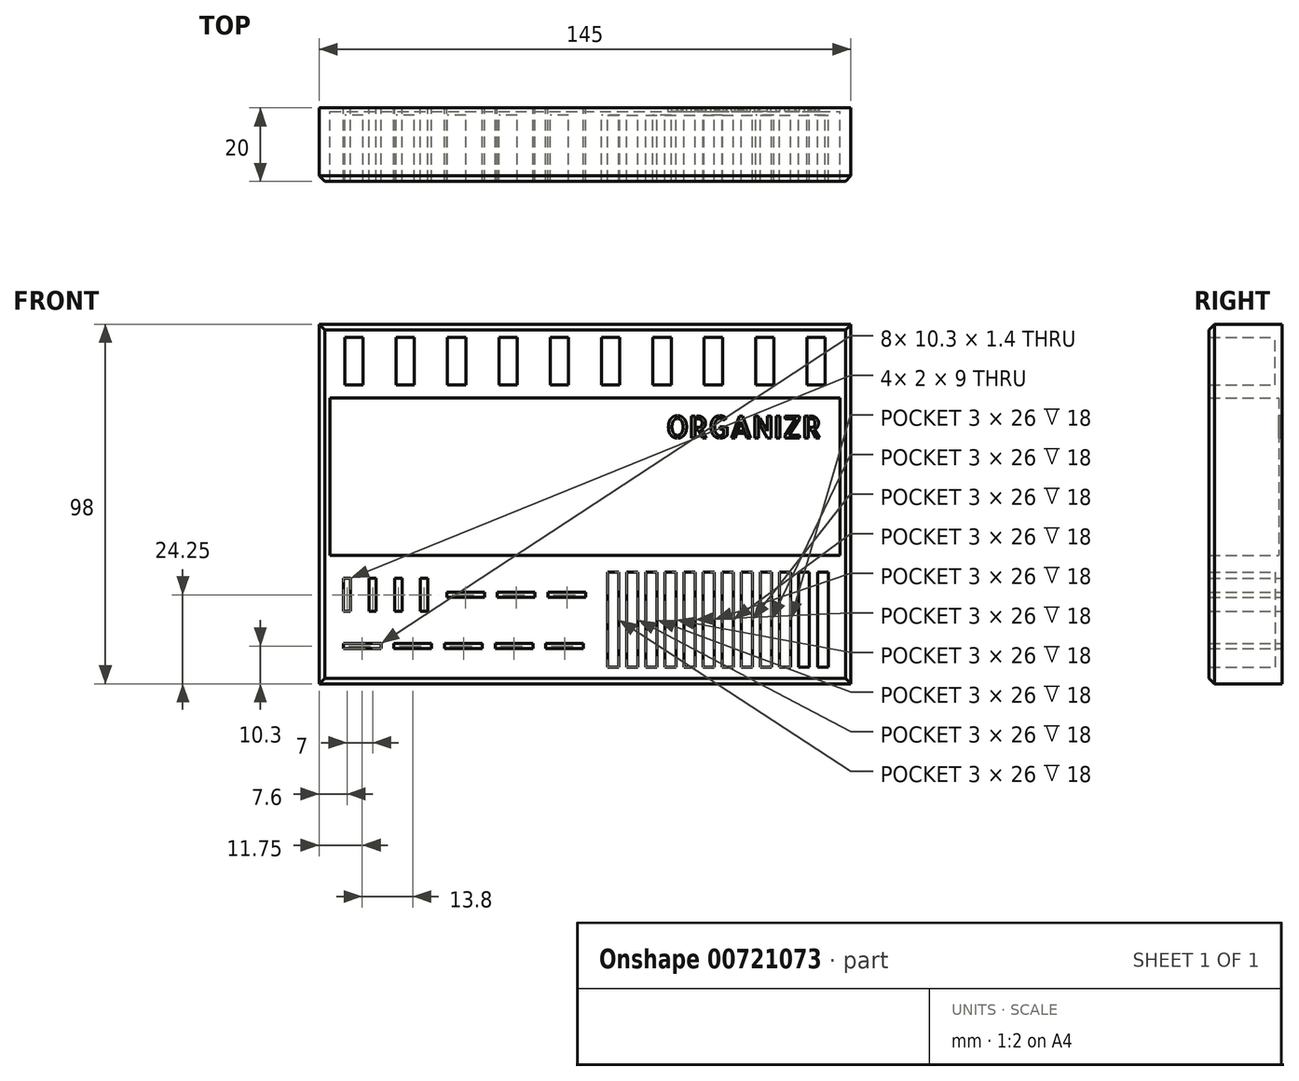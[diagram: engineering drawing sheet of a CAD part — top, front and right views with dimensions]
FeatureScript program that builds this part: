
annotation { "Feature Type Name" : "Feature", "Feature Type Description" : "" }
export const myFeature = defineFeature(function(context is Context, id is Id, definition is map)
    precondition{}
    {
        {
            var Q0;
            Q0=qCreatedBy(makeId("Front.planeOp"),FACE);
            var sketch = newSketch(context, id + "F0", { "sketchPlane" : qUnion([Q0])});
            skLineSegment(sketch, "E0.bottom", {"start": v(72.5, 49) * mm, "end": v(-72.5, 49) * mm});
            skLineSegment(sketch, "E0.top", {"start": v(72.5, -49) * mm, "end": v(-72.5, -49) * mm});
            skLineSegment(sketch, "E0.left", {"start": v(72.5, 49) * mm, "end": v(72.5, -49) * mm});
            skLineSegment(sketch, "E0.right", {"start": v(-72.5, 49) * mm, "end": v(-72.5, -49) * mm});
            skPoint(sketch, "E0.middle", {"position": v(0, 0) * mm});
            skLineSegment(sketch, "E1.bottom", {"start": v(-60.5, 32.5) * mm, "end": v(-65.5, 32.5) * mm});
            skLineSegment(sketch, "E1.top", {"start": v(-60.5, 45.5) * mm, "end": v(-65.5, 45.5) * mm});
            skLineSegment(sketch, "E1.left", {"start": v(-60.5, 32.5) * mm, "end": v(-60.5, 45.5) * mm});
            skLineSegment(sketch, "E1.right", {"start": v(-65.5, 32.5) * mm, "end": v(-65.5, 45.5) * mm});
            skPoint(sketch, "E1.middle", {"position": v(-63, 39) * mm});
            skLineSegment(sketch, "E2.bottom", {"start": v(-46.5, 32.5) * mm, "end": v(-51.5, 32.5) * mm});
            skLineSegment(sketch, "E2.top", {"start": v(-46.5, 45.5) * mm, "end": v(-51.5, 45.5) * mm});
            skLineSegment(sketch, "E2.left", {"start": v(-46.5, 32.5) * mm, "end": v(-46.5, 45.5) * mm});
            skLineSegment(sketch, "E2.right", {"start": v(-51.5, 32.5) * mm, "end": v(-51.5, 45.5) * mm});
            skLineSegment(sketch, "E3.bottom", {"start": v(-32.5, 32.5) * mm, "end": v(-37.5, 32.5) * mm});
            skLineSegment(sketch, "E3.top", {"start": v(-32.5, 45.5) * mm, "end": v(-37.5, 45.5) * mm});
            skLineSegment(sketch, "E3.left", {"start": v(-32.5, 32.5) * mm, "end": v(-32.5, 45.5) * mm});
            skLineSegment(sketch, "E3.right", {"start": v(-37.5, 32.5) * mm, "end": v(-37.5, 45.5) * mm});
            skLineSegment(sketch, "E4.bottom", {"start": v(-18.5, 32.5) * mm, "end": v(-23.5, 32.5) * mm});
            skLineSegment(sketch, "E4.top", {"start": v(-18.5, 45.5) * mm, "end": v(-23.5, 45.5) * mm});
            skLineSegment(sketch, "E4.left", {"start": v(-18.5, 32.5) * mm, "end": v(-18.5, 45.5) * mm});
            skLineSegment(sketch, "E4.right", {"start": v(-23.5, 32.5) * mm, "end": v(-23.5, 45.5) * mm});
            skLineSegment(sketch, "E5.bottom", {"start": v(-4.5, 32.5) * mm, "end": v(-9.5, 32.5) * mm});
            skLineSegment(sketch, "E5.top", {"start": v(-4.5, 45.5) * mm, "end": v(-9.5, 45.5) * mm});
            skLineSegment(sketch, "E5.left", {"start": v(-4.5, 32.5) * mm, "end": v(-4.5, 45.5) * mm});
            skLineSegment(sketch, "E5.right", {"start": v(-9.5, 32.5) * mm, "end": v(-9.5, 45.5) * mm});
            skPoint(sketch, "E5.middle", {"position": v(-7, 39) * mm});
            skLineSegment(sketch, "E6.bottom", {"start": v(9.5, 32.5) * mm, "end": v(4.5, 32.5) * mm});
            skLineSegment(sketch, "E6.top", {"start": v(9.5, 45.5) * mm, "end": v(4.5, 45.5) * mm});
            skLineSegment(sketch, "E6.left", {"start": v(9.5, 32.5) * mm, "end": v(9.5, 45.5) * mm});
            skLineSegment(sketch, "E6.right", {"start": v(4.5, 32.5) * mm, "end": v(4.5, 45.5) * mm});
            skLineSegment(sketch, "E7.bottom", {"start": v(23.5, 32.5) * mm, "end": v(18.5, 32.5) * mm});
            skLineSegment(sketch, "E7.top", {"start": v(23.5, 45.5) * mm, "end": v(18.5, 45.5) * mm});
            skLineSegment(sketch, "E7.left", {"start": v(23.5, 32.5) * mm, "end": v(23.5, 45.5) * mm});
            skLineSegment(sketch, "E7.right", {"start": v(18.5, 32.5) * mm, "end": v(18.5, 45.5) * mm});
            skLineSegment(sketch, "E8.bottom", {"start": v(37.5, 32.5) * mm, "end": v(32.5, 32.5) * mm});
            skLineSegment(sketch, "E8.top", {"start": v(37.5, 45.5) * mm, "end": v(32.5, 45.5) * mm});
            skLineSegment(sketch, "E8.left", {"start": v(37.5, 32.5) * mm, "end": v(37.5, 45.5) * mm});
            skLineSegment(sketch, "E8.right", {"start": v(32.5, 32.5) * mm, "end": v(32.5, 45.5) * mm});
            skLineSegment(sketch, "E9.bottom", {"start": v(51.5, 32.5) * mm, "end": v(46.5, 32.5) * mm});
            skLineSegment(sketch, "E9.top", {"start": v(51.5, 45.5) * mm, "end": v(46.5, 45.5) * mm});
            skLineSegment(sketch, "E9.left", {"start": v(51.5, 32.5) * mm, "end": v(51.5, 45.5) * mm});
            skLineSegment(sketch, "E9.right", {"start": v(46.5, 32.5) * mm, "end": v(46.5, 45.5) * mm});
            skLineSegment(sketch, "E10.bottom", {"start": v(65.5, 32.5) * mm, "end": v(60.5, 32.5) * mm});
            skLineSegment(sketch, "E10.top", {"start": v(65.5, 45.5) * mm, "end": v(60.5, 45.5) * mm});
            skLineSegment(sketch, "E10.left", {"start": v(65.5, 32.5) * mm, "end": v(65.5, 45.5) * mm});
            skLineSegment(sketch, "E10.right", {"start": v(60.5, 32.5) * mm, "end": v(60.5, 45.5) * mm});
            skLineSegment(sketch, "E11.bottom", {"start": v(-69.5, 29) * mm, "end": v(69.5, 29) * mm});
            skLineSegment(sketch, "E11.top", {"start": v(-69.5, -14) * mm, "end": v(69.5, -14) * mm});
            skLineSegment(sketch, "E11.left", {"start": v(-69.5, 29) * mm, "end": v(-69.5, -14) * mm});
            skLineSegment(sketch, "E11.right", {"start": v(69.5, 29) * mm, "end": v(69.5, -14) * mm});
            skLineSegment(sketch, "E12.bottom", {"start": v(63.4, -18.5) * mm, "end": v(66.4, -18.5) * mm});
            skLineSegment(sketch, "E12.top", {"start": v(63.4, -44.5) * mm, "end": v(66.4, -44.5) * mm});
            skLineSegment(sketch, "E12.left", {"start": v(63.4, -18.5) * mm, "end": v(63.4, -44.5) * mm});
            skLineSegment(sketch, "E12.right", {"start": v(66.4, -18.5) * mm, "end": v(66.4, -44.5) * mm});
            skLineSegment(sketch, "E13.bottom", {"start": v(58.2, -18.5) * mm, "end": v(61.2, -18.5) * mm});
            skLineSegment(sketch, "E13.top", {"start": v(58.2, -44.5) * mm, "end": v(61.2, -44.5) * mm});
            skLineSegment(sketch, "E13.left", {"start": v(58.2, -18.5) * mm, "end": v(58.2, -44.5) * mm});
            skLineSegment(sketch, "E13.right", {"start": v(61.2, -18.5) * mm, "end": v(61.2, -44.5) * mm});
            skLineSegment(sketch, "E14.bottom", {"start": v(53, -18.5) * mm, "end": v(56, -18.5) * mm});
            skLineSegment(sketch, "E14.top", {"start": v(53, -44.5) * mm, "end": v(56, -44.5) * mm});
            skLineSegment(sketch, "E14.left", {"start": v(53, -18.5) * mm, "end": v(53, -44.5) * mm});
            skLineSegment(sketch, "E14.right", {"start": v(56, -18.5) * mm, "end": v(56, -44.5) * mm});
            skLineSegment(sketch, "E15.bottom", {"start": v(47.8, -18.5) * mm, "end": v(50.8, -18.5) * mm});
            skLineSegment(sketch, "E15.top", {"start": v(47.8, -44.5) * mm, "end": v(50.8, -44.5) * mm});
            skLineSegment(sketch, "E15.left", {"start": v(47.8, -18.5) * mm, "end": v(47.8, -44.5) * mm});
            skLineSegment(sketch, "E15.right", {"start": v(50.8, -18.5) * mm, "end": v(50.8, -44.5) * mm});
            skLineSegment(sketch, "E16.bottom", {"start": v(42.6, -18.5) * mm, "end": v(45.6, -18.5) * mm});
            skLineSegment(sketch, "E16.top", {"start": v(42.6, -44.5) * mm, "end": v(45.6, -44.5) * mm});
            skLineSegment(sketch, "E16.left", {"start": v(42.6, -18.5) * mm, "end": v(42.6, -44.5) * mm});
            skLineSegment(sketch, "E16.right", {"start": v(45.6, -18.5) * mm, "end": v(45.6, -44.5) * mm});
            skLineSegment(sketch, "E17.bottom", {"start": v(37.4, -18.5) * mm, "end": v(40.4, -18.5) * mm});
            skLineSegment(sketch, "E17.top", {"start": v(37.4, -44.5) * mm, "end": v(40.4, -44.5) * mm});
            skLineSegment(sketch, "E17.left", {"start": v(37.4, -18.5) * mm, "end": v(37.4, -44.5) * mm});
            skLineSegment(sketch, "E17.right", {"start": v(40.4, -18.5) * mm, "end": v(40.4, -44.5) * mm});
            skLineSegment(sketch, "E18.bottom", {"start": v(32.2, -18.5) * mm, "end": v(35.2, -18.5) * mm});
            skLineSegment(sketch, "E18.top", {"start": v(32.2, -44.5) * mm, "end": v(35.2, -44.5) * mm});
            skLineSegment(sketch, "E18.left", {"start": v(32.2, -18.5) * mm, "end": v(32.2, -44.5) * mm});
            skLineSegment(sketch, "E18.right", {"start": v(35.2, -18.5) * mm, "end": v(35.2, -44.5) * mm});
            skLineSegment(sketch, "E19.bottom", {"start": v(27, -18.5) * mm, "end": v(30, -18.5) * mm});
            skLineSegment(sketch, "E19.top", {"start": v(27, -44.5) * mm, "end": v(30, -44.5) * mm});
            skLineSegment(sketch, "E19.left", {"start": v(27, -18.5) * mm, "end": v(27, -44.5) * mm});
            skLineSegment(sketch, "E19.right", {"start": v(30, -18.5) * mm, "end": v(30, -44.5) * mm});
            skLineSegment(sketch, "E20.bottom", {"start": v(21.8, -18.5) * mm, "end": v(24.8, -18.5) * mm});
            skLineSegment(sketch, "E20.top", {"start": v(21.8, -44.5) * mm, "end": v(24.8, -44.5) * mm});
            skLineSegment(sketch, "E20.left", {"start": v(21.8, -18.5) * mm, "end": v(21.8, -44.5) * mm});
            skLineSegment(sketch, "E20.right", {"start": v(24.8, -18.5) * mm, "end": v(24.8, -44.5) * mm});
            skLineSegment(sketch, "E21.bottom", {"start": v(16.6, -18.5) * mm, "end": v(19.6, -18.5) * mm});
            skLineSegment(sketch, "E21.top", {"start": v(16.6, -44.5) * mm, "end": v(19.6, -44.5) * mm});
            skLineSegment(sketch, "E21.left", {"start": v(16.6, -18.5) * mm, "end": v(16.6, -44.5) * mm});
            skLineSegment(sketch, "E21.right", {"start": v(19.6, -18.5) * mm, "end": v(19.6, -44.5) * mm});
            skLineSegment(sketch, "E22.bottom", {"start": v(11.4, -18.5) * mm, "end": v(14.4, -18.5) * mm});
            skLineSegment(sketch, "E22.top", {"start": v(11.4, -44.5) * mm, "end": v(14.4, -44.5) * mm});
            skLineSegment(sketch, "E22.left", {"start": v(11.4, -18.5) * mm, "end": v(11.4, -44.5) * mm});
            skLineSegment(sketch, "E22.right", {"start": v(14.4, -18.5) * mm, "end": v(14.4, -44.5) * mm});
            skLineSegment(sketch, "E23.bottom", {"start": v(6.2, -18.5) * mm, "end": v(9.2, -18.5) * mm});
            skLineSegment(sketch, "E23.top", {"start": v(6.2, -44.5) * mm, "end": v(9.2, -44.5) * mm});
            skLineSegment(sketch, "E23.left", {"start": v(6.2, -18.5) * mm, "end": v(6.2, -44.5) * mm});
            skLineSegment(sketch, "E23.right", {"start": v(9.2, -18.5) * mm, "end": v(9.2, -44.5) * mm});
            skLineSegment(sketch, "E24.bottom", {"start": v(0.2, -24.05) * mm, "end": v(-10.1, -24.05) * mm});
            skLineSegment(sketch, "E24.top", {"start": v(0.2, -25.45) * mm, "end": v(-10.1, -25.45) * mm});
            skLineSegment(sketch, "E24.left", {"start": v(0.2, -24.05) * mm, "end": v(0.2, -25.45) * mm});
            skLineSegment(sketch, "E24.right", {"start": v(-10.1, -24.05) * mm, "end": v(-10.1, -25.45) * mm});
            skLineSegment(sketch, "E25.bottom", {"start": v(-0.4, -38) * mm, "end": v(-10.7, -38) * mm});
            skLineSegment(sketch, "E25.top", {"start": v(-0.4, -39.4) * mm, "end": v(-10.7, -39.4) * mm});
            skLineSegment(sketch, "E25.left", {"start": v(-0.4, -38) * mm, "end": v(-0.4, -39.4) * mm});
            skLineSegment(sketch, "E25.right", {"start": v(-10.7, -38) * mm, "end": v(-10.7, -39.4) * mm});
            skLineSegment(sketch, "E26.bottom", {"start": v(-13.6, -24.05) * mm, "end": v(-23.9, -24.05) * mm});
            skLineSegment(sketch, "E26.top", {"start": v(-13.6, -25.45) * mm, "end": v(-23.9, -25.45) * mm});
            skLineSegment(sketch, "E26.left", {"start": v(-13.6, -24.05) * mm, "end": v(-13.6, -25.45) * mm});
            skLineSegment(sketch, "E26.right", {"start": v(-23.9, -24.05) * mm, "end": v(-23.9, -25.45) * mm});
            skLineSegment(sketch, "E27.bottom", {"start": v(-14.2, -38) * mm, "end": v(-24.5, -38) * mm});
            skLineSegment(sketch, "E27.top", {"start": v(-14.2, -39.4) * mm, "end": v(-24.5, -39.4) * mm});
            skLineSegment(sketch, "E27.left", {"start": v(-14.2, -38) * mm, "end": v(-14.2, -39.4) * mm});
            skLineSegment(sketch, "E27.right", {"start": v(-24.5, -38) * mm, "end": v(-24.5, -39.4) * mm});
            skLineSegment(sketch, "E28.bottom", {"start": v(-28, -38) * mm, "end": v(-38.3, -38) * mm});
            skLineSegment(sketch, "E28.top", {"start": v(-28, -39.4) * mm, "end": v(-38.3, -39.4) * mm});
            skLineSegment(sketch, "E28.left", {"start": v(-28, -38) * mm, "end": v(-28, -39.4) * mm});
            skLineSegment(sketch, "E28.right", {"start": v(-38.3, -38) * mm, "end": v(-38.3, -39.4) * mm});
            skLineSegment(sketch, "E29.bottom", {"start": v(-41.8, -38) * mm, "end": v(-52.1, -38) * mm});
            skLineSegment(sketch, "E29.top", {"start": v(-41.8, -39.4) * mm, "end": v(-52.1, -39.4) * mm});
            skLineSegment(sketch, "E29.left", {"start": v(-41.8, -38) * mm, "end": v(-41.8, -39.4) * mm});
            skLineSegment(sketch, "E29.right", {"start": v(-52.1, -38) * mm, "end": v(-52.1, -39.4) * mm});
            skLineSegment(sketch, "E30.bottom", {"start": v(-55.6, -38) * mm, "end": v(-65.9, -38) * mm});
            skLineSegment(sketch, "E30.top", {"start": v(-55.6, -39.4) * mm, "end": v(-65.9, -39.4) * mm});
            skLineSegment(sketch, "E30.left", {"start": v(-55.6, -38) * mm, "end": v(-55.6, -39.4) * mm});
            skLineSegment(sketch, "E30.right", {"start": v(-65.9, -38) * mm, "end": v(-65.9, -39.4) * mm});
            skLineSegment(sketch, "E31.bottom", {"start": v(-65.9, -20.25) * mm, "end": v(-63.9, -20.25) * mm});
            skLineSegment(sketch, "E31.top", {"start": v(-65.9, -29.25) * mm, "end": v(-63.9, -29.25) * mm});
            skLineSegment(sketch, "E31.left", {"start": v(-65.9, -20.25) * mm, "end": v(-65.9, -29.25) * mm});
            skLineSegment(sketch, "E31.right", {"start": v(-63.9, -20.25) * mm, "end": v(-63.9, -29.25) * mm});
            skLineSegment(sketch, "E32.bottom", {"start": v(-58.9, -20.25) * mm, "end": v(-56.9, -20.25) * mm});
            skLineSegment(sketch, "E32.top", {"start": v(-58.9, -29.25) * mm, "end": v(-56.9, -29.25) * mm});
            skLineSegment(sketch, "E32.left", {"start": v(-58.9, -20.25) * mm, "end": v(-58.9, -29.25) * mm});
            skLineSegment(sketch, "E32.right", {"start": v(-56.9, -20.25) * mm, "end": v(-56.9, -29.25) * mm});
            skLineSegment(sketch, "E33.bottom", {"start": v(-51.9, -20.25) * mm, "end": v(-49.9, -20.25) * mm});
            skLineSegment(sketch, "E33.top", {"start": v(-51.9, -29.25) * mm, "end": v(-49.9, -29.25) * mm});
            skLineSegment(sketch, "E33.left", {"start": v(-51.9, -20.25) * mm, "end": v(-51.9, -29.25) * mm});
            skLineSegment(sketch, "E33.right", {"start": v(-49.9, -20.25) * mm, "end": v(-49.9, -29.25) * mm});
            skLineSegment(sketch, "E34.bottom", {"start": v(-44.9, -20.25) * mm, "end": v(-42.9, -20.25) * mm});
            skLineSegment(sketch, "E34.top", {"start": v(-44.9, -29.25) * mm, "end": v(-42.9, -29.25) * mm});
            skLineSegment(sketch, "E34.left", {"start": v(-44.9, -20.25) * mm, "end": v(-44.9, -29.25) * mm});
            skLineSegment(sketch, "E34.right", {"start": v(-42.9, -20.25) * mm, "end": v(-42.9, -29.25) * mm});
            skText(sketch, "E35", { "text": "ORGANIZR", "fontName": "AllertaStencil-Regular.ttf"});
            skLineSegment(sketch, "E36.bottom", {"start": v(-27.4, -24.05) * mm, "end": v(-37.7, -24.05) * mm});
            skLineSegment(sketch, "E36.top", {"start": v(-27.4, -25.45) * mm, "end": v(-37.7, -25.45) * mm});
            skLineSegment(sketch, "E36.left", {"start": v(-27.4, -24.05) * mm, "end": v(-27.4, -25.45) * mm});
            skLineSegment(sketch, "E36.right", {"start": v(-37.7, -24.05) * mm, "end": v(-37.7, -25.45) * mm});
            const initialGuessF0  = {"E35": [0.0221, 0.01802, 1, 0, 0.00598]};
            skSetInitialGuess(sketch, initialGuessF0);
            skSolve(sketch);
        }
        {
            var Q0;
            Q0=makeQuery(id+"F0.imprint","IMPRINT",FACE,{"disambiguationData":[TD([[makeQuery(id+"F0.imprint","IMPRINT",EDGE,{"derivedFrom":sQuery(id+"F0.wireOp",EDGE,"E0.bottom")}),1.0]])]});
            extrude(context, id + "F1", {"entities" : qUnion([Q0]), "depth" : 20 * mm, "offsetDistance" : 25 * mm});
        }
        {
            var Q0;
            Q0=makeQuery(id+"F0.imprint","IMPRINT",FACE,{"disambiguationData":[TD([[makeQuery(id+"F0.imprint","IMPRINT",EDGE,{"derivedFrom":sQuery(id+"F0.wireOp",EDGE,"E11.bottom")}),-1.0]])]});
            extrude(context, id + "F2", {"entities" : qUnion([Q0]), "operationType" : NewBodyOperationType.ADD, "depth" : 1 * mm, "offsetDistance" : 25 * mm});
        }
        {
            var Q0;
            Q0=makeQuery(id+"F1.opExtrude","CAP_EDGE",EDGE,{"disambiguationData":[OSD([sQuery(id+"F0.wireOp",EDGE,"E0.right")])],"isStart":false});
            var Q1;
            Q1=makeQuery(id+"F1.opExtrude","CAP_EDGE",EDGE,{"disambiguationData":[OSD([sQuery(id+"F0.wireOp",EDGE,"E0.top")])],"isStart":false});
            var Q2;
            Q2=makeQuery(id+"F1.opExtrude","CAP_EDGE",EDGE,{"disambiguationData":[OSD([sQuery(id+"F0.wireOp",EDGE,"E0.bottom")])],"isStart":false});
            var Q3;
            Q3=makeQuery(id+"F1.opExtrude","CAP_EDGE",EDGE,{"disambiguationData":[OSD([sQuery(id+"F0.wireOp",EDGE,"E0.left")])],"isStart":false});
            chamfer(context, id + "F3", {"entities" : qUnion([Q0, Q1, Q2, Q3]), "width" : 1.5 * mm, "tangentPropagation" : true});
        }
        {
            var Q0;
            Q0=qCreatedBy(makeId("Front.planeOp"),FACE);
            var sketch = newSketch(context, id + "F4", { "sketchPlane" : qUnion([Q0])});
            skLineSegment(sketch, "E37.bottom", {"start": v(9.2, -18.49) * mm, "end": v(65.5, -18.49) * mm});
            skLineSegment(sketch, "E37.top", {"start": v(9.2, -44.5) * mm, "end": v(65.5, -44.5) * mm});
            skLineSegment(sketch, "E37.left", {"start": v(9.2, -18.49) * mm, "end": v(9.2, -44.5) * mm});
            skLineSegment(sketch, "E37.right", {"start": v(65.5, -18.49) * mm, "end": v(65.5, -44.5) * mm});
            skSolve(sketch);
        }
        {
            var Q0;
            Q0=qCreatedBy(makeId("Front.planeOp"),FACE);
            var sketch = newSketch(context, id + "F5", { "sketchPlane" : qUnion([Q0])});
            skLineSegment(sketch, "E38.bottom", {"start": v(5.27, -18.03) * mm, "end": v(67.27, -18.03) * mm});
            skLineSegment(sketch, "E38.top", {"start": v(5.27, -44.91) * mm, "end": v(67.27, -44.91) * mm});
            skLineSegment(sketch, "E38.left", {"start": v(5.27, -18.03) * mm, "end": v(5.27, -44.91) * mm});
            skLineSegment(sketch, "E38.right", {"start": v(67.27, -18.03) * mm, "end": v(67.27, -44.91) * mm});
            skLineSegment(sketch, "E39.bottom", {"start": v(-66.5, 46) * mm, "end": v(66.5, 46) * mm});
            skLineSegment(sketch, "E39.top", {"start": v(-66.5, 32) * mm, "end": v(66.5, 32) * mm});
            skLineSegment(sketch, "E39.left", {"start": v(-66.5, 46) * mm, "end": v(-66.5, 32) * mm});
            skLineSegment(sketch, "E39.right", {"start": v(66.5, 46) * mm, "end": v(66.5, 32) * mm});
            skSolve(sketch);
        }
        {
            var Q0;
            Q0 = qSketchRegion(id + "F5", true);
            extrude(context, id + "F6", {"entities" : qUnion([Q0]), "operationType" : NewBodyOperationType.ADD, "depth" : 2 * mm, "offsetDistance" : 25 * mm});
        }
    });
